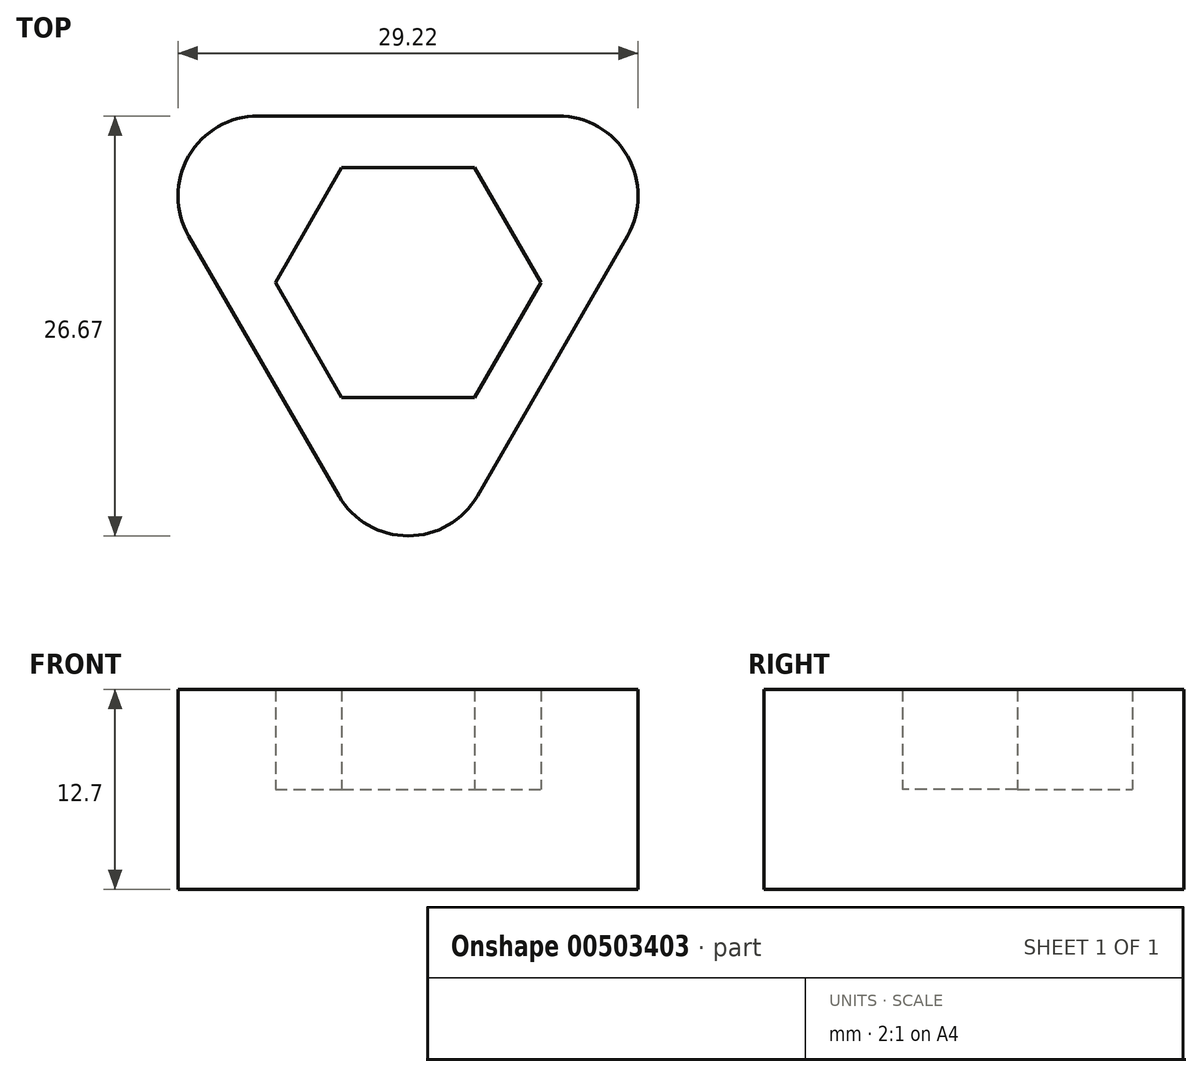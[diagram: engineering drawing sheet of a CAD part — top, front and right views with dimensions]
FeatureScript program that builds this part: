
annotation { "Feature Type Name" : "Feature", "Feature Type Description" : "" }
export const myFeature = defineFeature(function(context is Context, id is Id, definition is map)
    precondition{}
    {
        {
            var Q0;
            Q0=qCreatedBy(makeId("Top.planeOp"),FACE);
            var sketch = newSketch(context, id + "F0", { "sketchPlane" : qUnion([Q0])});
            skCircle(sketch, "E0.cCircle", {"center": v(0, 0) * mm, "radius": 7.3 * mm, "construction": true});
            skLineSegment(sketch, "E0.0", {"start": v(-4.22, 7.3) * mm, "end": v(4.22, 7.3) * mm});
            skLineSegment(sketch, "E0.1", {"start": v(4.22, 7.3) * mm, "end": v(8.43, 0) * mm});
            skLineSegment(sketch, "E0.2", {"start": v(8.43, 0) * mm, "end": v(4.22, -7.3) * mm});
            skLineSegment(sketch, "E0.3", {"start": v(4.22, -7.3) * mm, "end": v(-4.22, -7.3) * mm});
            skLineSegment(sketch, "E0.4", {"start": v(-4.22, -7.3) * mm, "end": v(-8.43, 0) * mm});
            skLineSegment(sketch, "E0.5", {"start": v(-8.43, 0) * mm, "end": v(-4.22, 7.3) * mm});
            skPoint(sketch, "E0.0.midPoint", {"position": v(0, 7.3) * mm});
            skCircle(sketch, "E1.cCircle", {"center": v(0, 0) * mm, "radius": 10.58 * mm, "construction": true});
            skLineSegment(sketch, "E1.0", {"start": v(-18.33, 10.58) * mm, "end": v(18.33, 10.58) * mm});
            skLineSegment(sketch, "E1.1", {"start": v(18.33, 10.58) * mm, "end": v(0, -21.17) * mm});
            skLineSegment(sketch, "E1.2", {"start": v(0, -21.17) * mm, "end": v(-18.33, 10.58) * mm});
            skPoint(sketch, "E1.0.midPoint", {"position": v(0, 10.58) * mm});
            skSolve(sketch);
        }
        {
            var Q0;
            Q0=makeQuery(id+"F0.imprint","IMPRINT",FACE,{"disambiguationData":[TD([[makeQuery(id+"F0.imprint","IMPRINT",EDGE,{"derivedFrom":sQuery(id+"F0.wireOp",EDGE,"E0.0")}),1.0]])]});
            extrude(context, id + "F1", {"entities" : qUnion([Q0]), "depth" : 6.35 * mm});
        }
        {
            var Q0;
            Q0 = qSketchRegion(id + "F0", true);
            extrude(context, id + "F2", {"entities" : qUnion([Q0]), "operationType" : NewBodyOperationType.ADD, "depth" : 12.7 * mm});
        }
        {
            var Q0;
            Q0=makeQuery(id+"F1.opExtrude","CAP_FACE",FACE,{"disambiguationData":[OSD([sQuery(id+"F0.wireOp",EDGE,"E0.0"),sQuery(id+"F0.wireOp",EDGE,"E0.1"),sQuery(id+"F0.wireOp",EDGE,"E0.2"),sQuery(id+"F0.wireOp",EDGE,"E0.3"),sQuery(id+"F0.wireOp",EDGE,"E0.4"),sQuery(id+"F0.wireOp",EDGE,"E0.5"),sQuery(id+"F0.wireOp",EDGE,"E1.0"),sQuery(id+"F0.wireOp",EDGE,"E1.1"),sQuery(id+"F0.wireOp",EDGE,"E1.2")])],"isStart":true});
            var sketch = newSketch(context, id + "F3", { "sketchPlane" : qUnion([Q0])});
            skCircle(sketch, "E2.cCircle", {"center": v(0, 0) * mm, "radius": 7.3 * mm, "construction": true});
            skLineSegment(sketch, "E2.0", {"start": v(4.22, -7.3) * mm, "end": v(-4.22, -7.3) * mm});
            skLineSegment(sketch, "E2.1", {"start": v(-4.22, -7.3) * mm, "end": v(-8.43, 0) * mm});
            skLineSegment(sketch, "E2.2", {"start": v(-8.43, 0) * mm, "end": v(-4.22, 7.3) * mm});
            skLineSegment(sketch, "E2.3", {"start": v(-4.22, 7.3) * mm, "end": v(4.22, 7.3) * mm});
            skLineSegment(sketch, "E2.4", {"start": v(4.22, 7.3) * mm, "end": v(8.43, 0) * mm});
            skLineSegment(sketch, "E2.5", {"start": v(8.43, 0) * mm, "end": v(4.22, -7.3) * mm});
            skPoint(sketch, "E2.0.midPoint", {"position": v(0, -7.3) * mm});
            skSolve(sketch);
        }
        {
            var Q0;
            Q0 = qSketchRegion(id + "F3", true);
            extrude(context, id + "F4", {"entities" : qUnion([Q0]), "operationType" : NewBodyOperationType.ADD, "oppositeDirection" : true, "depth" : 6.35 * mm});
        }
        {
            var Q0;
            {var subQ0=sQuery(id+"F0.wireOp",EDGE,"E1.1");var subQ1=sQuery(id+"F0.wireOp",EDGE,"E1.0");Q0=makeQuery(id+"F2.boolean.opBoolean","MERGE",EDGE,{"derivedFrom":[makeQuery(id+"F1.opExtrude","SWEPT_EDGE",EDGE,{"disambiguationData":[OSD([subQ1,subQ0])]}),makeQuery(id+"F2.opExtrude","SWEPT_EDGE",EDGE,{"disambiguationData":[OSD([subQ1,subQ0])]})]});}
            var Q1;
            {var subQ0=sQuery(id+"F0.wireOp",EDGE,"E1.2");var subQ1=sQuery(id+"F0.wireOp",EDGE,"E1.0");Q1=makeQuery(id+"F2.boolean.opBoolean","MERGE",EDGE,{"derivedFrom":[makeQuery(id+"F1.opExtrude","SWEPT_EDGE",EDGE,{"disambiguationData":[OSD([subQ1,subQ0])]}),makeQuery(id+"F2.opExtrude","SWEPT_EDGE",EDGE,{"disambiguationData":[OSD([subQ1,subQ0])]})]});}
            var Q2;
            {var subQ0=sQuery(id+"F0.wireOp",EDGE,"E1.2");var subQ1=sQuery(id+"F0.wireOp",EDGE,"E1.1");Q2=makeQuery(id+"F2.boolean.opBoolean","MERGE",EDGE,{"derivedFrom":[makeQuery(id+"F1.opExtrude","SWEPT_EDGE",EDGE,{"disambiguationData":[OSD([subQ1,subQ0])]}),makeQuery(id+"F2.opExtrude","SWEPT_EDGE",EDGE,{"disambiguationData":[OSD([subQ1,subQ0])]})]});}
            fillet(context, id + "F5", {"entities" : qUnion([Q0, Q1, Q2]), "radius" : 5.08 * mm, "tangentPropagation" : true, "allowEdgeOverflow" : false});
        }
    });
